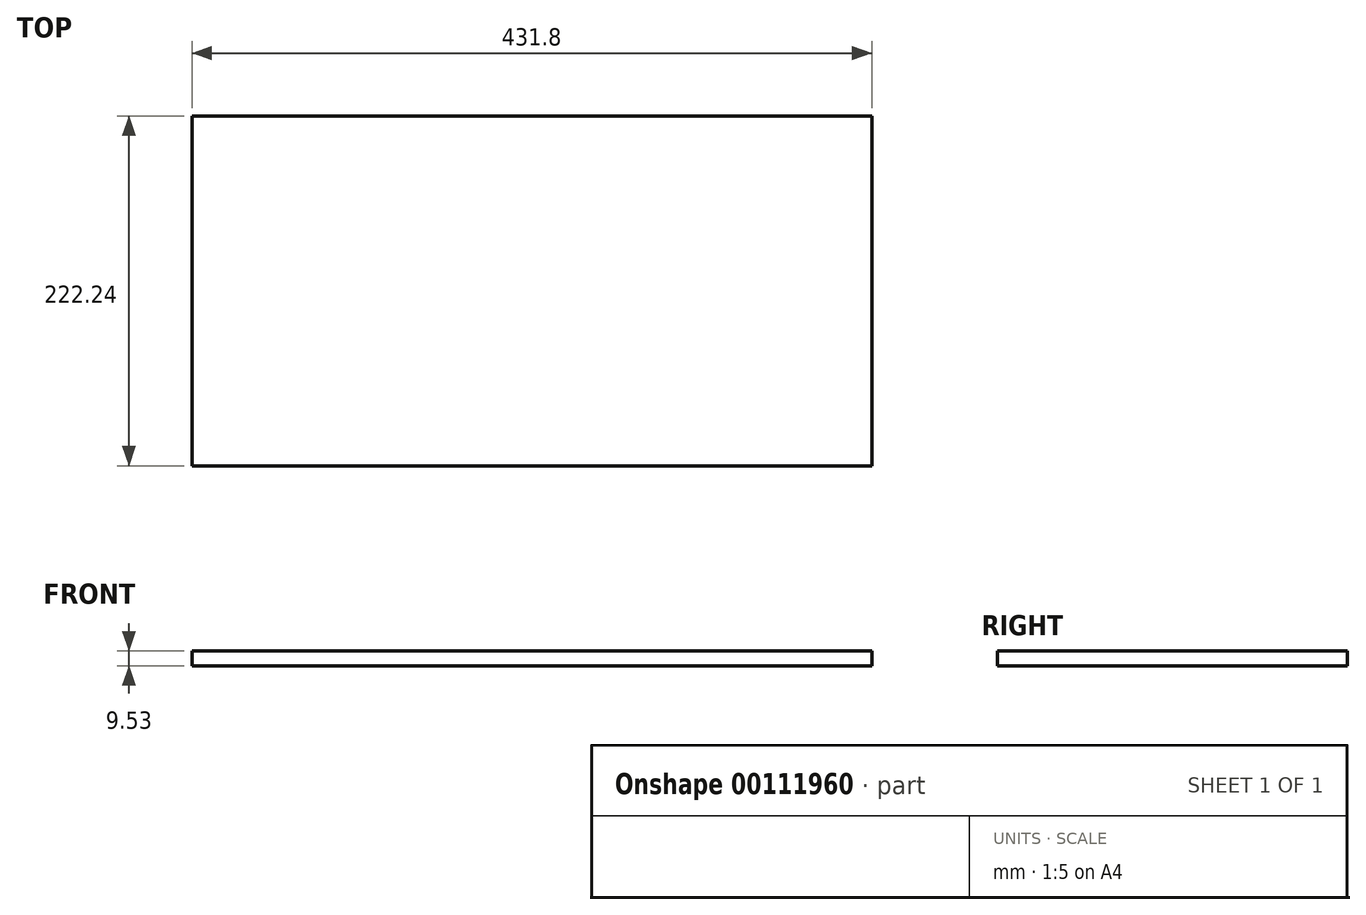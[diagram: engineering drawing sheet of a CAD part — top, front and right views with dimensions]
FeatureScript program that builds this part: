
annotation { "Feature Type Name" : "Feature", "Feature Type Description" : "" }
export const myFeature = defineFeature(function(context is Context, id is Id, definition is map)
    precondition{}
    {
        {
            var Q0;
            Q0=qCreatedBy(makeId("Top.planeOp"),FACE);
            var sketch = newSketch(context, id + "F0", { "sketchPlane" : qUnion([Q0])});
            skLineSegment(sketch, "E0.bottom", {"start": v(-215.9, 111.13) * mm, "end": v(215.9, 111.13) * mm});
            skLineSegment(sketch, "E0.top", {"start": v(-215.9, -111.12) * mm, "end": v(215.9, -111.12) * mm});
            skLineSegment(sketch, "E0.left", {"start": v(-215.9, 111.13) * mm, "end": v(-215.9, -111.13) * mm});
            skLineSegment(sketch, "E0.right", {"start": v(215.9, 111.13) * mm, "end": v(215.9, -111.13) * mm});
            skPoint(sketch, "E0.middle", {"position": v(0, 0) * mm});
            skSolve(sketch);
        }
        {
            var Q0;
            Q0=makeQuery(id+"F0.imprint","IMPRINT",FACE,{"disambiguationData":[TD([[makeQuery(id+"F0.imprint","IMPRINT",EDGE,{"derivedFrom":sQuery(id+"F0.wireOp",EDGE,"E0.bottom")}),-1.0]])]});
            extrude(context, id + "F1", {"entities" : qUnion([Q0]), "depth" : 9.52 * mm});
        }
    });
